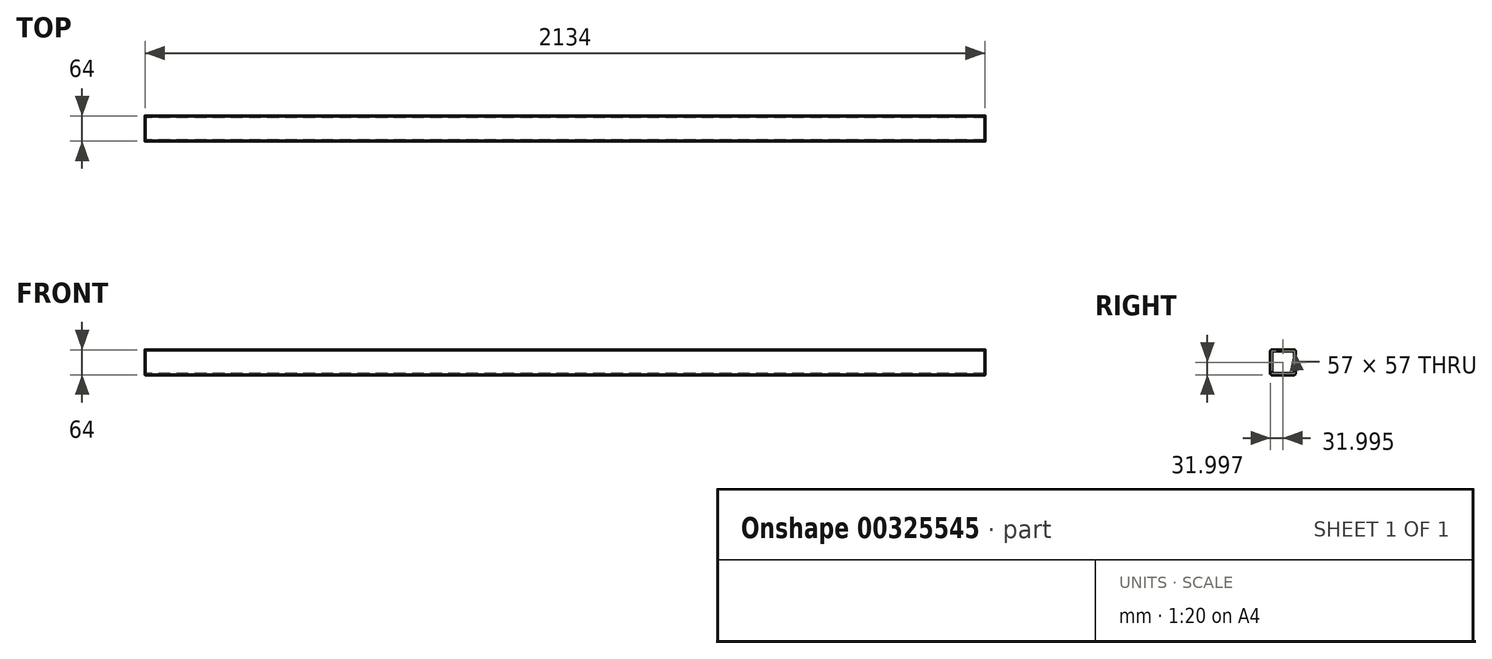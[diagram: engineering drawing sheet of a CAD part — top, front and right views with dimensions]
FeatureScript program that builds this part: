
annotation { "Feature Type Name" : "Feature", "Feature Type Description" : "" }
export const myFeature = defineFeature(function(context is Context, id is Id, definition is map)
    precondition{}
    {
        {
            var Q0;
            Q0=qCreatedBy(makeId("Right.planeOp"),FACE);
            var sketch = newSketch(context, id + "F0", { "sketchPlane" : qUnion([Q0])});
            skLineSegment(sketch, "E0.bottom", {"start": v(-37.46, 46) * mm, "end": v(16.54, 46) * mm});
            skLineSegment(sketch, "E0.top", {"start": v(-37.46, -18) * mm, "end": v(16.54, -18) * mm});
            skLineSegment(sketch, "E0.left", {"start": v(-42.46, 41) * mm, "end": v(-42.46, -13) * mm});
            skLineSegment(sketch, "E0.right", {"start": v(21.54, 41) * mm, "end": v(21.54, -13) * mm});
            skPoint(sketch, "E1.visualSharp", {"position": v(-42.46, 46) * mm});
            skArc(sketch, "E1.filletArc", {"start": v(-37.46, 46) * mm, "mid": v(-41, 44.54) * mm, "end": v(-42.46, 41) * mm});
            skPoint(sketch, "E2.visualSharp", {"position": v(21.54, 46) * mm});
            skArc(sketch, "E2.filletArc", {"start": v(21.54, 41) * mm, "mid": v(20.07, 44.54) * mm, "end": v(16.54, 46) * mm});
            skPoint(sketch, "E3.visualSharp", {"position": v(21.54, -18) * mm});
            skArc(sketch, "E3.filletArc", {"start": v(16.54, -18) * mm, "mid": v(20.07, -16.53) * mm, "end": v(21.54, -13) * mm});
            skPoint(sketch, "E4.visualSharp", {"position": v(-42.46, -18) * mm});
            skArc(sketch, "E4.filletArc", {"start": v(-42.46, -13) * mm, "mid": v(-41, -16.53) * mm, "end": v(-37.46, -18) * mm});
            skLineSegment(sketch, "E5.0", {"start": v(18.04, 42.5) * mm, "end": v(18.04, -14.5) * mm});
            skLineSegment(sketch, "E5.1", {"start": v(-38.96, 42.5) * mm, "end": v(18.04, 42.5) * mm});
            skLineSegment(sketch, "E5.2", {"start": v(-38.96, 42.5) * mm, "end": v(-38.96, -14.5) * mm});
            skLineSegment(sketch, "E5.3", {"start": v(-38.96, -14.5) * mm, "end": v(18.04, -14.5) * mm});
            skSolve(sketch);
        }
        {
            var Q0;
            Q0=makeQuery(id+"F0.imprint","IMPRINT",FACE,{"disambiguationData":[TD([[makeQuery(id+"F0.imprint","IMPRINT",EDGE,{"derivedFrom":sQuery(id+"F0.wireOp",EDGE,"E0.bottom")}),-1.0]])]});
            extrude(context, id + "F1", {"entities" : qUnion([Q0]), "depth" : 2134 * mm});
        }
    });
